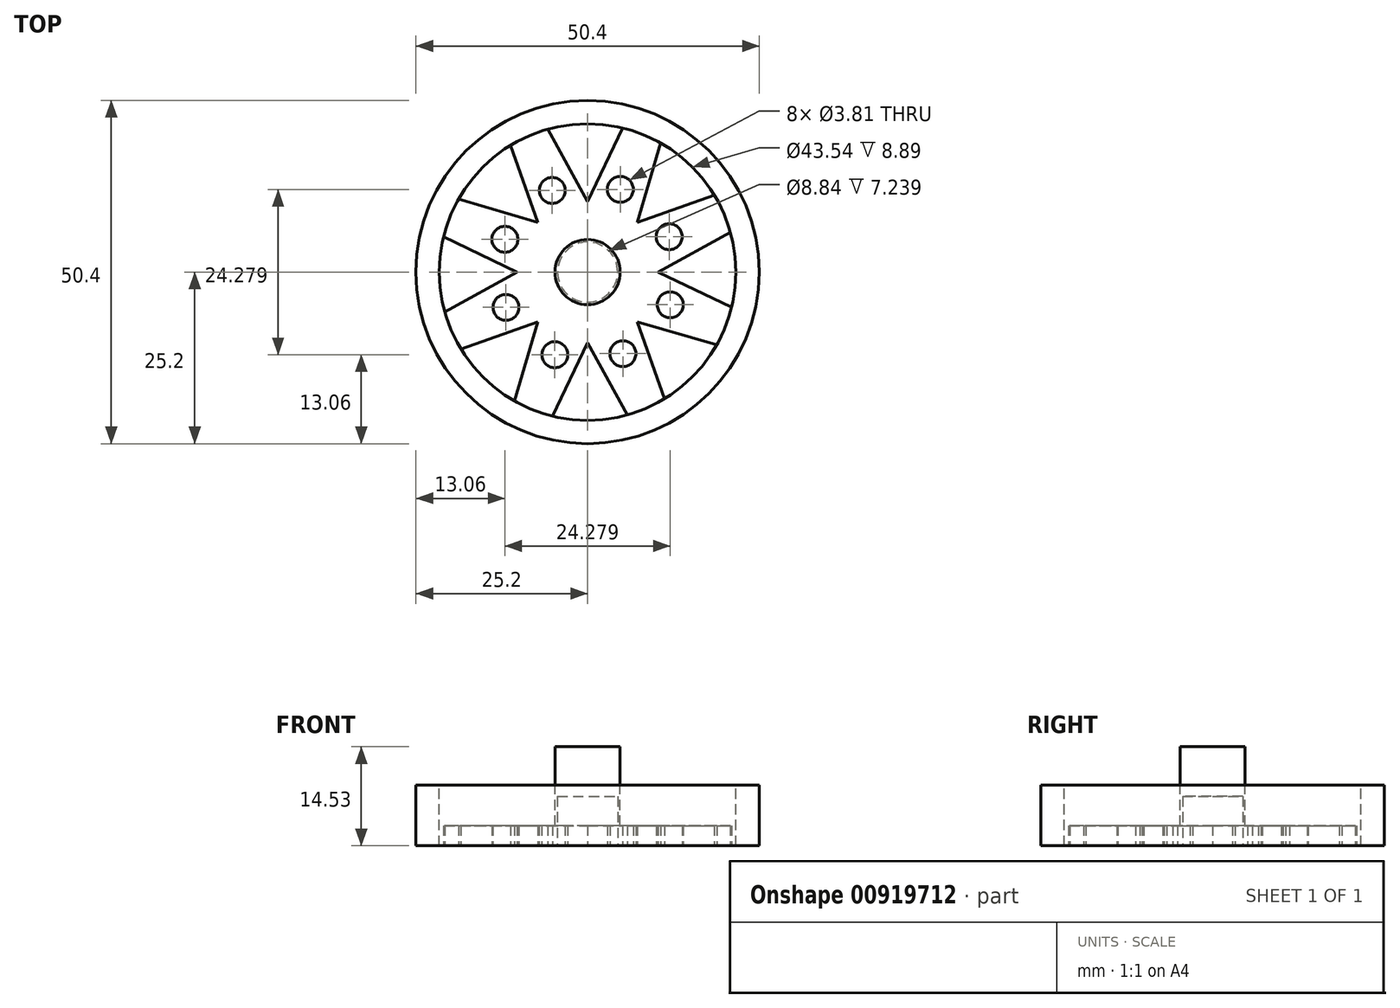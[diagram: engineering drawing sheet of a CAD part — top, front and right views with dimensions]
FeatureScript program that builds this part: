
annotation { "Feature Type Name" : "Feature", "Feature Type Description" : "" }
export const myFeature = defineFeature(function(context is Context, id is Id, definition is map)
    precondition{}
    {
        {
            var Q0;
            Q0=qCreatedBy(makeId("Front.planeOp"),FACE);
            var sketch = newSketch(context, id + "F0", { "sketchPlane" : qUnion([Q0])});
            skLineSegment(sketch, "E0", {"start": v(0, 16.7) * mm, "end": v(-4.79, 16.7) * mm});
            skLineSegment(sketch, "E1", {"start": v(-4.79, 16.7) * mm, "end": v(-4.79, 5.12) * mm});
            skLineSegment(sketch, "E2", {"start": v(-4.79, 5.12) * mm, "end": v(-21.77, 5.12) * mm});
            skLineSegment(sketch, "E3", {"start": v(-21.77, 5.12) * mm, "end": v(-21.77, 11.07) * mm});
            skLineSegment(sketch, "E4", {"start": v(-21.77, 11.07) * mm, "end": v(-25.2, 11.07) * mm});
            skLineSegment(sketch, "E5", {"start": v(-25.2, 11.07) * mm, "end": v(-25.2, 2.18) * mm});
            skLineSegment(sketch, "E6", {"start": v(-25.2, 2.18) * mm, "end": v(0, 2.18) * mm});
            skLineSegment(sketch, "E7", {"start": v(0, 16.7) * mm, "end": v(0, 2.18) * mm});
            skSolve(sketch);
        }
        {
            var Q0;
            Q0=makeQuery(id+"F0.imprint","IMPRINT",FACE,{"disambiguationData":[TD([[makeQuery(id+"F0.imprint","IMPRINT",EDGE,{"derivedFrom":sQuery(id+"F0.wireOp",EDGE,"E0")}),1.0]])]});
            var Q1;
            Q1=sQuery(id+"F0.wireOp",EDGE,"E7");
            revolve(context, id + "F1", {"surfaceOperationType" : NewSurfaceOperationType.NEW, "entities" : qUnion([Q0]), "axis" : qUnion([Q1]), "revolveType" : RevolveType.FULL});
        }
        {
            var Q0;
            Q0=makeQuery(id+"F1.opRevolve","SWEPT_FACE",FACE,{"disambiguationData":[OSD([sQuery(id+"F0.wireOp",EDGE,"E6")])]});
            var sketch = newSketch(context, id + "F2", { "sketchPlane" : qUnion([Q0])});
            skLineSegment(sketch, "E8", {"start": v(-5.17, 21.15) * mm, "end": v(0, 10.34) * mm});
            skLineSegment(sketch, "E9", {"start": v(0, 10.34) * mm, "end": v(5.83, 20.97) * mm});
            skCircle(sketch, "E10.0", {"center": v(0, 0) * mm, "radius": 21.77 * mm});
            skLineSegment(sketch, "E11.1.0", {"start": v(-18.6, 11.3) * mm, "end": v(-7.3, 7.3) * mm});
            skLineSegment(sketch, "E11.1.1", {"start": v(-7.3, 7.3) * mm, "end": v(-10.7, 18.95) * mm});
            skLineSegment(sketch, "E11.2.0", {"start": v(-21.15, -5.17) * mm, "end": v(-10.34, 0) * mm});
            skLineSegment(sketch, "E11.2.1", {"start": v(-10.34, 0) * mm, "end": v(-20.97, 5.83) * mm});
            skLineSegment(sketch, "E11.3.0", {"start": v(-11.3, -18.6) * mm, "end": v(-7.3, -7.3) * mm});
            skLineSegment(sketch, "E11.3.1", {"start": v(-7.3, -7.3) * mm, "end": v(-18.95, -10.7) * mm});
            skLineSegment(sketch, "E11.4.0", {"start": v(5.17, -21.15) * mm, "end": v(0, -10.34) * mm});
            skLineSegment(sketch, "E11.4.1", {"start": v(0, -10.34) * mm, "end": v(-5.83, -20.97) * mm});
            skLineSegment(sketch, "E11.5.0", {"start": v(18.6, -11.3) * mm, "end": v(7.3, -7.3) * mm});
            skLineSegment(sketch, "E11.5.1", {"start": v(7.3, -7.3) * mm, "end": v(10.7, -18.95) * mm});
            skLineSegment(sketch, "E11.6.0", {"start": v(21.15, 5.17) * mm, "end": v(10.34, 0) * mm});
            skLineSegment(sketch, "E11.6.1", {"start": v(10.34, 0) * mm, "end": v(20.97, -5.83) * mm});
            skLineSegment(sketch, "E11.7.0", {"start": v(11.3, 18.6) * mm, "end": v(7.3, 7.3) * mm});
            skLineSegment(sketch, "E11.7.1", {"start": v(7.3, 7.3) * mm, "end": v(18.95, 10.7) * mm});
            skSolve(sketch);
        }
        {
            var Q0;
            {var subQ0=sQuery(id+"F2.wireOp",EDGE,"E11.1.0");Q0=makeQuery(id+"F2.imprint","IMPRINT",FACE,{"disambiguationData":[TD([[makeQuery(id+"F2.imprint","IMPRINT",EDGE,{"derivedFrom":subQ0}),1.0]])]});}
            var Q1;
            {var subQ0=sQuery(id+"F2.wireOp",EDGE,"E8");Q1=makeQuery(id+"F2.imprint","IMPRINT",FACE,{"disambiguationData":[TD([[makeQuery(id+"F2.imprint","IMPRINT",EDGE,{"derivedFrom":subQ0}),1.0]])]});}
            var Q2;
            {var subQ0=sQuery(id+"F2.wireOp",EDGE,"E11.7.0");Q2=makeQuery(id+"F2.imprint","IMPRINT",FACE,{"disambiguationData":[TD([[makeQuery(id+"F2.imprint","IMPRINT",EDGE,{"derivedFrom":subQ0}),1.0]])]});}
            var Q3;
            {var subQ0=sQuery(id+"F2.wireOp",EDGE,"E11.6.0");Q3=makeQuery(id+"F2.imprint","IMPRINT",FACE,{"disambiguationData":[TD([[makeQuery(id+"F2.imprint","IMPRINT",EDGE,{"derivedFrom":subQ0}),1.0]])]});}
            var Q4;
            {var subQ0=sQuery(id+"F2.wireOp",EDGE,"E11.5.0");Q4=makeQuery(id+"F2.imprint","IMPRINT",FACE,{"disambiguationData":[TD([[makeQuery(id+"F2.imprint","IMPRINT",EDGE,{"derivedFrom":subQ0}),1.0]])]});}
            var Q5;
            {var subQ0=sQuery(id+"F2.wireOp",EDGE,"E11.4.0");Q5=makeQuery(id+"F2.imprint","IMPRINT",FACE,{"disambiguationData":[TD([[makeQuery(id+"F2.imprint","IMPRINT",EDGE,{"derivedFrom":subQ0}),1.0]])]});}
            var Q6;
            {var subQ0=sQuery(id+"F2.wireOp",EDGE,"E11.3.0");Q6=makeQuery(id+"F2.imprint","IMPRINT",FACE,{"disambiguationData":[TD([[makeQuery(id+"F2.imprint","IMPRINT",EDGE,{"derivedFrom":subQ0}),1.0]])]});}
            var Q7;
            {var subQ0=sQuery(id+"F2.wireOp",EDGE,"E11.2.0");Q7=makeQuery(id+"F2.imprint","IMPRINT",FACE,{"disambiguationData":[TD([[makeQuery(id+"F2.imprint","IMPRINT",EDGE,{"derivedFrom":subQ0}),1.0]])]});}
            extrude(context, id + "F3", {"entities" : qUnion([Q0, Q1, Q2, Q3, Q4, Q5, Q6, Q7]), "operationType" : NewBodyOperationType.REMOVE, "oppositeDirection" : true, "depth" : 25.4 * mm, "offsetDistance" : 25.4 * mm});
        }
        {
            var Q0;
            Q0=makeQuery(id+"F1.opRevolve","SWEPT_FACE",FACE,{"disambiguationData":[OSD([sQuery(id+"F0.wireOp",EDGE,"E6")])]});
            var sketch = newSketch(context, id + "F4", { "sketchPlane" : qUnion([Q0])});
            skCircle(sketch, "E12", {"center": v(4.8, -12.14) * mm, "radius": 1.9 * mm});
            skLineSegment(sketch, "E13", {"start": v(10.7, -18.95) * mm, "end": v(5.17, -21.15) * mm});
            skLineSegment(sketch, "E14", {"start": v(0, 0) * mm, "end": v(7.94, -20.05) * mm});
            skCircle(sketch, "E15.1.0", {"center": v(11.98, -5.19) * mm, "radius": 1.9 * mm});
            skCircle(sketch, "E15.2.0", {"center": v(12.14, 4.8) * mm, "radius": 1.9 * mm});
            skCircle(sketch, "E15.3.0", {"center": v(5.19, 11.98) * mm, "radius": 1.9 * mm});
            skCircle(sketch, "E15.4.0", {"center": v(-4.8, 12.14) * mm, "radius": 1.9 * mm});
            skCircle(sketch, "E15.5.0", {"center": v(-11.98, 5.19) * mm, "radius": 1.9 * mm});
            skCircle(sketch, "E15.6.0", {"center": v(-12.14, -4.8) * mm, "radius": 1.9 * mm});
            skCircle(sketch, "E15.7.0", {"center": v(-5.19, -11.98) * mm, "radius": 1.9 * mm});
            skPoint(sketch, "E15.center", {"position": v(0, 0) * mm});
            skSolve(sketch);
        }
        {
            var Q0;
            Q0=makeQuery(id+"F4.imprint","IMPRINT",FACE,{"disambiguationData":[TD([[makeQuery(id+"F4.imprint","IMPRINT",EDGE,{"derivedFrom":sQuery(id+"F4.wireOp",EDGE,"E15.1.0")}),1.0]])]});
            var Q1;
            {var subQ0=sQuery(id+"F4.wireOp",EDGE,"E14");var subQ1=sQuery(id+"F4.wireOp",EDGE,"E12");var subQ2=makeQuery(id+"F4.imprint","INTERSECT",VERTEX,{"disambiguationData":[OD(0.0)],"derivedFrom":[subQ1,subQ0]});Q1=makeQuery(id+"F4.imprint","IMPRINT",FACE,{"disambiguationData":[TD([[makeQuery(id+"F4.imprint","IMPRINT",EDGE,{"disambiguationData":[TD([[subQ2,-1.0]])],"derivedFrom":subQ1}),1.0]])]});}
            var Q2;
            {var subQ0=sQuery(id+"F4.wireOp",EDGE,"E14");var subQ1=sQuery(id+"F4.wireOp",EDGE,"E12");var subQ2=makeQuery(id+"F4.imprint","INTERSECT",VERTEX,{"disambiguationData":[OD(0.0)],"derivedFrom":[subQ1,subQ0]});Q2=makeQuery(id+"F4.imprint","IMPRINT",FACE,{"disambiguationData":[TD([[makeQuery(id+"F4.imprint","IMPRINT",EDGE,{"disambiguationData":[TD([[subQ2,1.0]])],"derivedFrom":subQ1}),1.0]])]});}
            var Q3;
            Q3=makeQuery(id+"F4.imprint","IMPRINT",FACE,{"disambiguationData":[TD([[makeQuery(id+"F4.imprint","IMPRINT",EDGE,{"derivedFrom":sQuery(id+"F4.wireOp",EDGE,"E15.7.0")}),1.0]])]});
            var Q4;
            Q4=makeQuery(id+"F4.imprint","IMPRINT",FACE,{"disambiguationData":[TD([[makeQuery(id+"F4.imprint","IMPRINT",EDGE,{"derivedFrom":sQuery(id+"F4.wireOp",EDGE,"E15.6.0")}),1.0]])]});
            var Q5;
            Q5=makeQuery(id+"F4.imprint","IMPRINT",FACE,{"disambiguationData":[TD([[makeQuery(id+"F4.imprint","IMPRINT",EDGE,{"derivedFrom":sQuery(id+"F4.wireOp",EDGE,"E15.5.0")}),1.0]])]});
            var Q6;
            Q6=makeQuery(id+"F4.imprint","IMPRINT",FACE,{"disambiguationData":[TD([[makeQuery(id+"F4.imprint","IMPRINT",EDGE,{"derivedFrom":sQuery(id+"F4.wireOp",EDGE,"E15.4.0")}),1.0]])]});
            var Q7;
            Q7=makeQuery(id+"F4.imprint","IMPRINT",FACE,{"disambiguationData":[TD([[makeQuery(id+"F4.imprint","IMPRINT",EDGE,{"derivedFrom":sQuery(id+"F4.wireOp",EDGE,"E15.3.0")}),1.0]])]});
            var Q8;
            Q8=makeQuery(id+"F4.imprint","IMPRINT",FACE,{"disambiguationData":[TD([[makeQuery(id+"F4.imprint","IMPRINT",EDGE,{"derivedFrom":sQuery(id+"F4.wireOp",EDGE,"E15.2.0")}),1.0]])]});
            extrude(context, id + "F5", {"entities" : qUnion([Q0, Q1, Q2, Q3, Q4, Q5, Q6, Q7, Q8]), "operationType" : NewBodyOperationType.REMOVE, "oppositeDirection" : true, "depth" : 25.4 * mm, "offsetDistance" : 25.4 * mm});
        }
        {
            var Q0;
            Q0=makeQuery(id+"F1.opRevolve","SWEPT_FACE",FACE,{"disambiguationData":[OSD([sQuery(id+"F0.wireOp",EDGE,"E6")])]});
            var sketch = newSketch(context, id + "F6", { "sketchPlane" : qUnion([Q0])});
            skCircle(sketch, "E16", {"center": v(0, 0) * mm, "radius": 4.42 * mm});
            skSolve(sketch);
        }
        {
            var Q0;
            Q0=makeQuery(id+"F6.imprint","IMPRINT",FACE,{"disambiguationData":[TD([[makeQuery(id+"F6.imprint","IMPRINT",EDGE,{"derivedFrom":sQuery(id+"F6.wireOp",EDGE,"E16")}),1.0]])]});
            extrude(context, id + "F7", {"entities" : qUnion([Q0]), "operationType" : NewBodyOperationType.REMOVE, "oppositeDirection" : true, "depth" : 7.24 * mm, "offsetDistance" : 25.4 * mm});
        }
    });
